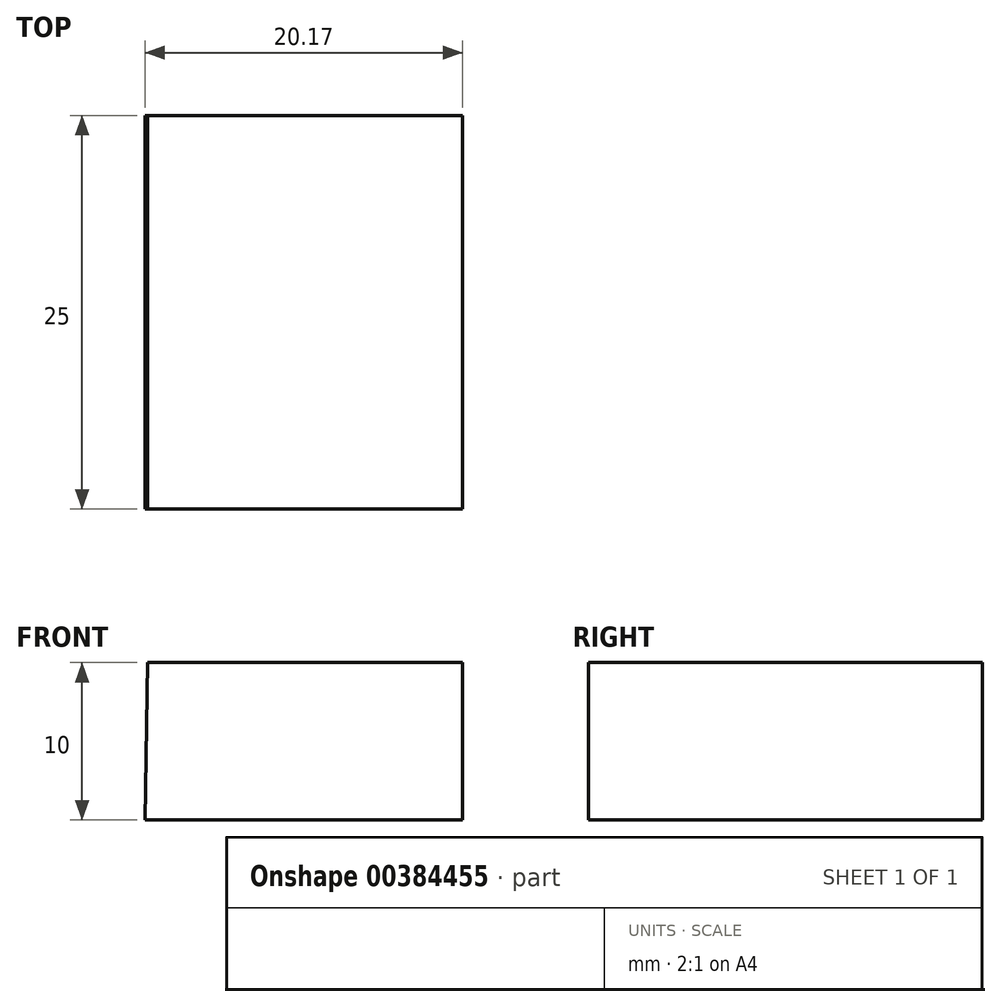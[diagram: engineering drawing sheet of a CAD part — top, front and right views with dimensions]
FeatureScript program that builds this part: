
annotation { "Feature Type Name" : "Feature", "Feature Type Description" : "" }
export const myFeature = defineFeature(function(context is Context, id is Id, definition is map)
    precondition{}
    {
        {
            var Q0;
            Q0=qCreatedBy(makeId("Front.planeOp"),FACE);
            var sketch = newSketch(context, id + "F0", { "sketchPlane" : qUnion([Q0])});
            skLineSegment(sketch, "E0", {"start": v(-12.53, 5.04) * mm, "end": v(7.47, 5.04) * mm});
            skLineSegment(sketch, "E1", {"start": v(7.47, 5.04) * mm, "end": v(7.47, -4.96) * mm});
            skLineSegment(sketch, "E2", {"start": v(7.47, -4.96) * mm, "end": v(-12.7, -4.96) * mm});
            skLineSegment(sketch, "E3", {"start": v(-12.7, -4.96) * mm, "end": v(-12.53, 5.04) * mm});
            skSolve(sketch);
        }
        {
            var Q0;
            Q0=makeQuery(id+"F0.imprint","IMPRINT",FACE,{"disambiguationData":[TD([[makeQuery(id+"F0.imprint","IMPRINT",EDGE,{"derivedFrom":sQuery(id+"F0.wireOp",EDGE,"E0")}),-1.0]])]});
            extrude(context, id + "F1", {"entities" : qUnion([Q0]), "depth" : 25 * mm, "offsetDistance" : 25 * mm});
        }
    });
